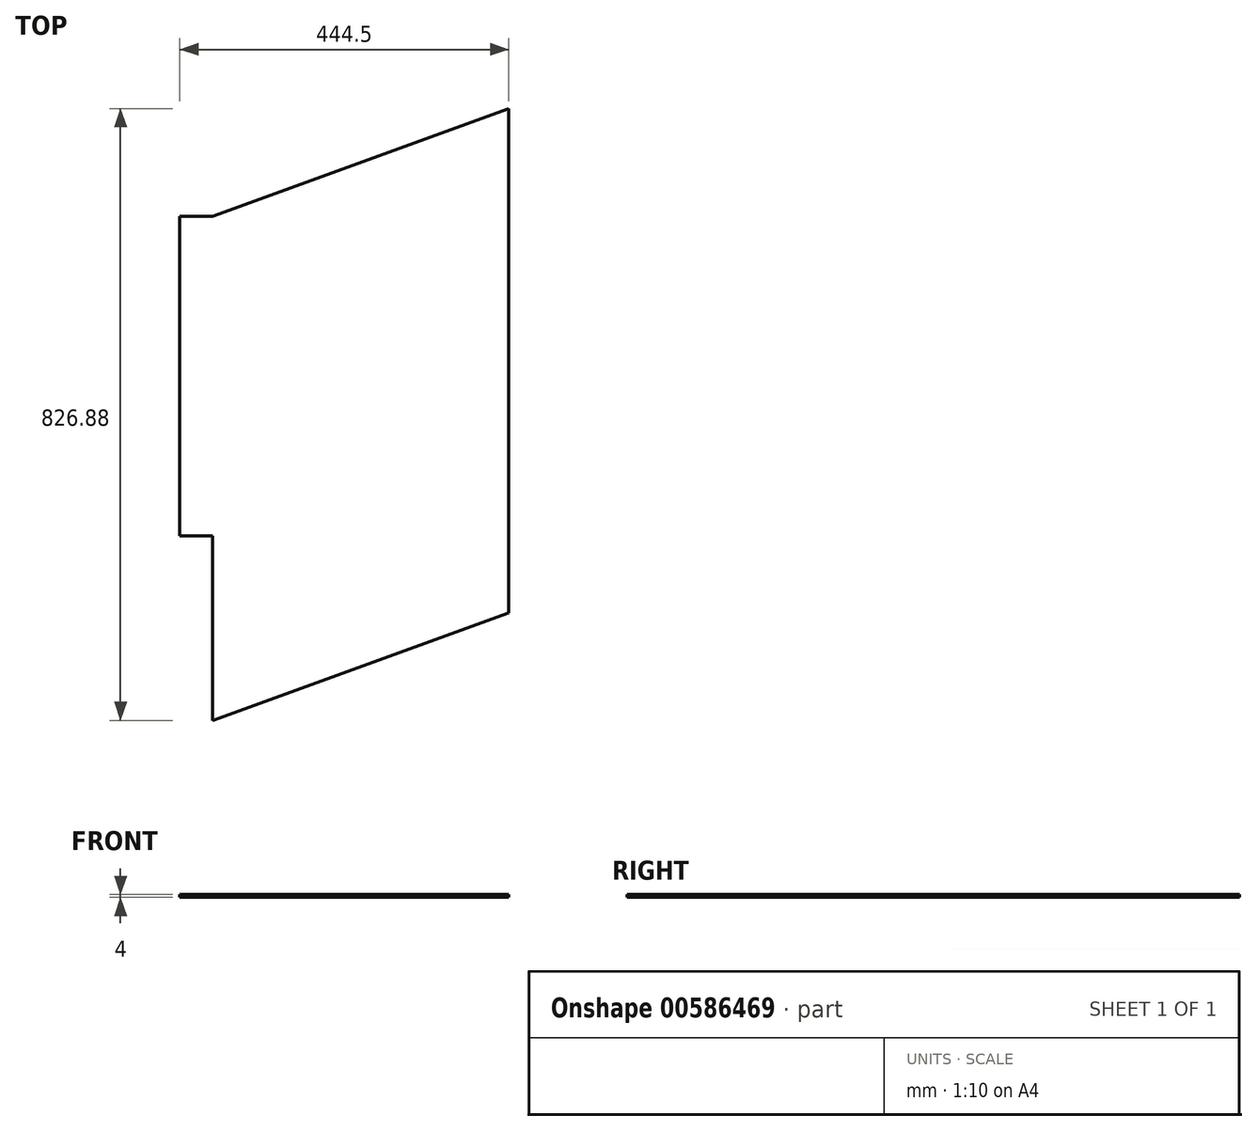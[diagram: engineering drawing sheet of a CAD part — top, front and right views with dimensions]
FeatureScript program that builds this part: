
annotation { "Feature Type Name" : "Feature", "Feature Type Description" : "" }
export const myFeature = defineFeature(function(context is Context, id is Id, definition is map)
    precondition{}
    {
        {
            var Q0;
            Q0=qCreatedBy(makeId("Top.planeOp"),FACE);
            var sketch = newSketch(context, id + "F0", { "sketchPlane" : qUnion([Q0])});
            skLineSegment(sketch, "E0.bottom", {"start": v(-200.03, -215.9) * mm, "end": v(-155.57, -215.9) * mm});
            skLineSegment(sketch, "E0.top", {"start": v(-200.03, 215.9) * mm, "end": v(200.02, 215.9) * mm});
            skLineSegment(sketch, "E0.left", {"start": v(-200.03, -215.9) * mm, "end": v(-200.03, 215.9) * mm});
            skLineSegment(sketch, "E0.right", {"start": v(200.03, -215.9) * mm, "end": v(200.03, 215.9) * mm});
            skLineSegment(sketch, "E1", {"start": v(-155.58, 17.4) * mm, "end": v(-155.57, -215.9) * mm});
            skLineSegment(sketch, "E2", {"start": v(-111.13, 1.21) * mm, "end": v(-111.12, -215.9) * mm});
            skLineSegment(sketch, "E3", {"start": v(-66.68, -14.96) * mm, "end": v(-66.67, -215.9) * mm});
            skLineSegment(sketch, "E4", {"start": v(-22.23, -31.14) * mm, "end": v(-22.22, -215.9) * mm});
            skLineSegment(sketch, "E5", {"start": v(66.68, -63.5) * mm, "end": v(66.68, -215.9) * mm});
            skLineSegment(sketch, "E6", {"start": v(-111.12, -215.9) * mm, "end": v(-66.67, -215.9) * mm});
            skLineSegment(sketch, "E7", {"start": v(-155.57, -215.9) * mm, "end": v(-111.12, -215.9) * mm});
            skLineSegment(sketch, "E8", {"start": v(-66.67, -215.9) * mm, "end": v(-22.22, -215.9) * mm});
            skLineSegment(sketch, "E9", {"start": v(-22.22, -215.9) * mm, "end": v(66.67, -215.9) * mm});
            skLineSegment(sketch, "E10", {"start": v(66.67, -215.9) * mm, "end": v(200.03, -215.9) * mm});
            skLineSegment(sketch, "E11", {"start": v(-200.03, 215.9) * mm, "end": v(-244.48, 215.9) * mm});
            skLineSegment(sketch, "E12", {"start": v(-244.48, 215.9) * mm, "end": v(-244.47, -215.9) * mm});
            skLineSegment(sketch, "E13", {"start": v(-244.48, -215.9) * mm, "end": v(-200.03, -215.9) * mm});
            skLineSegment(sketch, "E14", {"start": v(200.02, 361.5) * mm, "end": v(200.03, 215.9) * mm});
            skLineSegment(sketch, "E15", {"start": v(-200.03, 0) * mm, "end": v(-66.67, 0) * mm, "construction": true});
            skLineSegment(sketch, "E16", {"start": v(-66.67, 0) * mm, "end": v(66.68, 0) * mm, "construction": true});
            skLineSegment(sketch, "E17", {"start": v(66.68, 0) * mm, "end": v(200.03, 0) * mm, "construction": true});
            skPoint(sketch, "E18", {"position": v(0, 0) * mm});
            skLineSegment(sketch, "E19", {"start": v(-200.03, 33.57) * mm, "end": v(200.03, -112.04) * mm});
            skLineSegment(sketch, "E20.bottom", {"start": v(76.2, -66.67) * mm, "end": v(190.5, -66.67) * mm, "construction": true});
            skLineSegment(sketch, "E20.top", {"start": v(76.2, -206.37) * mm, "end": v(190.5, -206.37) * mm, "construction": true});
            skLineSegment(sketch, "E20.left", {"start": v(76.2, -66.67) * mm, "end": v(76.2, -206.37) * mm, "construction": true});
            skLineSegment(sketch, "E20.right", {"start": v(190.5, -66.67) * mm, "end": v(190.5, -206.37) * mm, "construction": true});
            skLineSegment(sketch, "E21", {"start": v(133.35, -215.9) * mm, "end": v(133.35, -206.38) * mm, "construction": true});
            skLineSegment(sketch, "E22", {"start": v(190.5, -136.52) * mm, "end": v(200.02, -136.52) * mm, "construction": true});
            skLineSegment(sketch, "E23", {"start": v(200.03, 361.5) * mm, "end": v(-200.03, 215.9) * mm});
            skSolve(sketch);
        }
        {
            var Q0;
            Q0=qCreatedBy(makeId("Top.planeOp"),FACE);
            var sketch = newSketch(context, id + "F1", { "sketchPlane" : qUnion([Q0])});
            skLineSegment(sketch, "E24.0", {"start": v(-200.03, 33.57) * mm, "end": v(200.03, -112.04) * mm, "construction": true});
            skLineSegment(sketch, "E25.MirrorCS", {"start": v(-200.03, -465.37) * mm, "end": v(200.03, -319.76) * mm});
            skLineSegment(sketch, "E26.0", {"start": v(-244.48, 215.9) * mm, "end": v(-244.47, -215.9) * mm});
            skLineSegment(sketch, "E27.0", {"start": v(200.03, 361.5) * mm, "end": v(-200.03, 215.9) * mm});
            skLineSegment(sketch, "E28.0", {"start": v(-200.03, 215.9) * mm, "end": v(-244.48, 215.9) * mm});
            skLineSegment(sketch, "E29.0", {"start": v(200.02, 361.5) * mm, "end": v(200.03, 215.9) * mm});
            skLineSegment(sketch, "E30.0", {"start": v(200.03, -215.9) * mm, "end": v(200.03, 215.9) * mm});
            skLineSegment(sketch, "E31.0", {"start": v(-244.48, -215.9) * mm, "end": v(-200.03, -215.9) * mm});
            skLineSegment(sketch, "E32", {"start": v(-200.03, -215.9) * mm, "end": v(-200.03, -465.37) * mm});
            skLineSegment(sketch, "E33", {"start": v(200.03, -319.76) * mm, "end": v(200.03, -215.9) * mm});
            skSolve(sketch);
        }
        {
            var Q0;
            Q0 = qSketchRegion(id + "F1", true);
            extrude(context, id + "F2", {"entities" : qUnion([Q0]), "depth" : 4 * mm, "offsetDistance" : 25.4 * mm});
        }
    });
